# Revit family: R-TA-040
name_source: partatom
category: Modèles génériques
units: mm (PartAtom-declared; Revit-internal decimal feet)

## family parameters
Conserver l'orientation des annotations = Non
Cote de connecteur circulaire = Utiliser le diamètre
Couper avec des vides une fois chargée = Non
Hôte = Mur
Partagée = Non
Peut héberger une armature = Non
Repère de localisation dans la pièce = Non
Toujours verticalement = Oui
Type d'élément = Normal

## types (1)
- TA-040
    Acoustique = RW (C ; Ctr) = 38(-1 ; -5)
    Description = Trappe de visite 1 vantail verticale, EI15, 38(-1; -5) dB, avec cadre/huisserie monobloc MDF
    Décalage panneau = 32 mm  [stored 0.104987 ft]
    Elévation par défaut = 0 mm  [stored 0 ft]
    Fabricant = MALERBA
    Fiche_Produit = TA-040
    Hauteur Reservation = 400 mm  [stored 1.31234 ft]
    Hauteur appuit = 1056 mm
    Huisserie = <Par catégorie>
    Jeu = 2 mm  [stored 0.00656168 ft]
    Jeu hôte = 5 mm  [stored 0.0164042 ft]
    Largeur /2 = 150 mm  [stored 0.492126 ft]
    Largeur Reservation = 300 mm  [stored 0.984252 ft]
    Materiaux_Dominant = MDF
    Note d'identification = TRAPPES EI15 VERTICALE CADRE MONOBLOC MDF 38dB
    Panneau = <Par catégorie>
    Reference_Commerciale = T EI15 VAc
    Resistance_Feu = E15-EI15
    Sens_Feu = Recto/Verso
    URL = https://www.malerba.fr

note: [stored X ft] marks values corroborated as IEEE doubles in the binary element streams (Revit-internal decimal feet)

## geometry (parser evidence)
native form markers: Blend x12
no freeform markers — native parametric forms only
